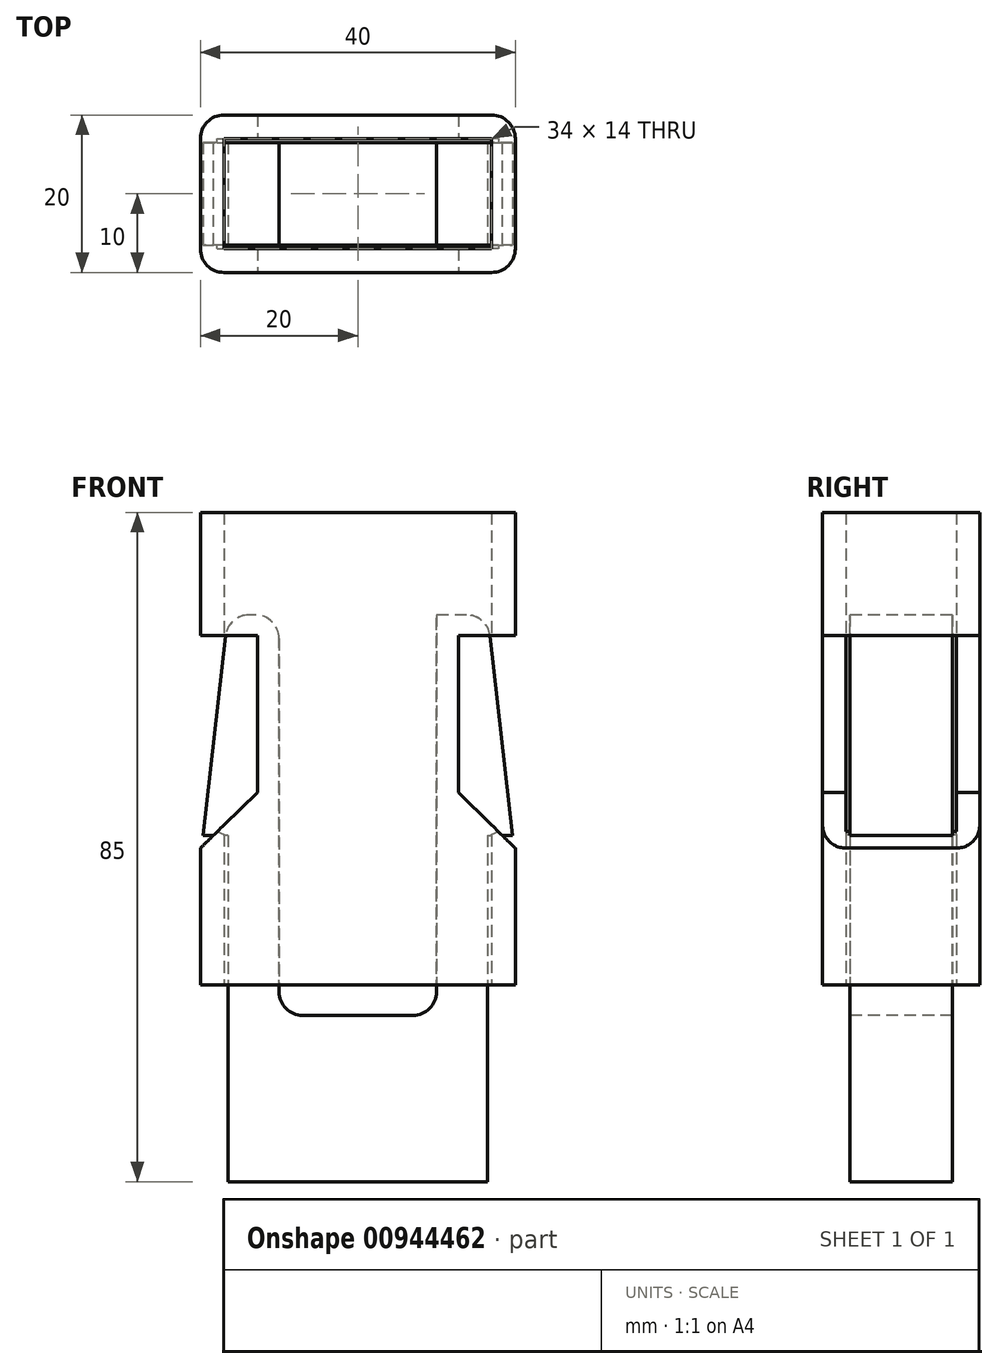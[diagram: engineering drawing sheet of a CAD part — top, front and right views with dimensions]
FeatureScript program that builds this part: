
annotation { "Feature Type Name" : "Feature", "Feature Type Description" : "" }
export const myFeature = defineFeature(function(context is Context, id is Id, definition is map)
    precondition{}
    {
        {
            var Q0;
            Q0=qCreatedBy(makeId("Top.planeOp"),FACE);
            var sketch = newSketch(context, id + "F0", { "sketchPlane" : qUnion([Q0])});
            skLineSegment(sketch, "E0.bottom", {"start": v(17, -10) * mm, "end": v(-17, -10) * mm});
            skLineSegment(sketch, "E0.top", {"start": v(17, 10) * mm, "end": v(-17, 10) * mm});
            skLineSegment(sketch, "E0.left", {"start": v(20, -7) * mm, "end": v(20, 7) * mm});
            skLineSegment(sketch, "E0.right", {"start": v(-20, -7) * mm, "end": v(-20, 7) * mm});
            skPoint(sketch, "E0.middle", {"position": v(0, 0) * mm});
            skPoint(sketch, "E1.visualSharp", {"position": v(-20, 10) * mm});
            skArc(sketch, "E1.filletArc", {"start": v(-17, 10) * mm, "mid": v(-19.12, 9.12) * mm, "end": v(-20, 7) * mm});
            skPoint(sketch, "E2.visualSharp", {"position": v(20, 10) * mm});
            skArc(sketch, "E2.filletArc", {"start": v(20, 7) * mm, "mid": v(19.12, 9.12) * mm, "end": v(17, 10) * mm});
            skPoint(sketch, "E3.visualSharp", {"position": v(20, -10) * mm});
            skArc(sketch, "E3.filletArc", {"start": v(17, -10) * mm, "mid": v(19.12, -9.12) * mm, "end": v(20, -7) * mm});
            skPoint(sketch, "E4.visualSharp", {"position": v(-20, -10) * mm});
            skArc(sketch, "E4.filletArc", {"start": v(-20, -7) * mm, "mid": v(-19.12, -9.12) * mm, "end": v(-17, -10) * mm});
            skLineSegment(sketch, "E5.0", {"start": v(17, 7) * mm, "end": v(-17, 7) * mm});
            skLineSegment(sketch, "E6.0", {"start": v(-17, -7) * mm, "end": v(-17, 7) * mm});
            skLineSegment(sketch, "E7.0", {"start": v(17, -7) * mm, "end": v(-17, -7) * mm});
            skLineSegment(sketch, "E8.0", {"start": v(17, -7) * mm, "end": v(17, 7) * mm});
            skSolve(sketch);
        }
        {
            var Q0;
            Q0=makeQuery(id+"F0.imprint","IMPRINT",FACE,{"disambiguationData":[TD([[makeQuery(id+"F0.imprint","IMPRINT",EDGE,{"derivedFrom":sQuery(id+"F0.wireOp",EDGE,"E0.bottom")}),-1.0]])]});
            extrude(context, id + "F1", {"entities" : qUnion([Q0]), "depth" : 60 * mm, "offsetDistance" : 25 * mm});
        }
        {
            var Q0;
            Q0=qCreatedBy(makeId("Front.planeOp"),FACE);
            var sketch = newSketch(context, id + "F2", { "sketchPlane" : qUnion([Q0])});
            skLineSegment(sketch, "E9", {"start": v(-22.85, 14.58) * mm, "end": v(-12.76, 24.45) * mm});
            skLineSegment(sketch, "E10", {"start": v(-12.76, 24.45) * mm, "end": v(-12.76, 44.4) * mm});
            skLineSegment(sketch, "E11", {"start": v(-12.76, 44.4) * mm, "end": v(-25.04, 44.4) * mm});
            skLineSegment(sketch, "E12", {"start": v(-25.04, 44.4) * mm, "end": v(-22.85, 14.58) * mm});
            skLineSegment(sketch, "E13.MirrorCS", {"start": v(25.04, 44.4) * mm, "end": v(22.85, 14.58) * mm});
            skLineSegment(sketch, "E14.MirrorCS", {"start": v(12.76, 44.4) * mm, "end": v(25.04, 44.4) * mm});
            skLineSegment(sketch, "E15.MirrorCS", {"start": v(12.76, 24.45) * mm, "end": v(12.76, 44.4) * mm});
            skLineSegment(sketch, "E16.MirrorCS", {"start": v(22.85, 14.58) * mm, "end": v(12.76, 24.45) * mm});
            skSolve(sketch);
        }
        {
            var Q0;
            Q0=makeQuery(id+"F2.imprint","IMPRINT",FACE,{"disambiguationData":[TD([[makeQuery(id+"F2.imprint","IMPRINT",EDGE,{"derivedFrom":sQuery(id+"F2.wireOp",EDGE,"E9")}),1.0]])]});
            var Q1;
            Q1=makeQuery(id+"F2.imprint","IMPRINT",FACE,{"disambiguationData":[TD([[makeQuery(id+"F2.imprint","IMPRINT",EDGE,{"derivedFrom":sQuery(id+"F2.wireOp",EDGE,"E13.MirrorCS")}),-1.0]])]});
            extrude(context, id + "F3", {"entities" : qUnion([Q0, Q1]), "operationType" : NewBodyOperationType.REMOVE, "endBound" : BoundingType.SYMMETRIC, "oppositeDirection" : true, "depth" : 25 * mm, "offsetDistance" : 25 * mm});
        }
        {
            var Q0;
            Q0=makeQuery(id+"F1.opExtrude","CAP_FACE",FACE,{"disambiguationData":[OSD([sQuery(id+"F0.wireOp",EDGE,"E0.bottom"),sQuery(id+"F0.wireOp",EDGE,"E0.top"),sQuery(id+"F0.wireOp",EDGE,"E0.left"),sQuery(id+"F0.wireOp",EDGE,"E0.right"),sQuery(id+"F0.wireOp",EDGE,"E1.filletArc"),sQuery(id+"F0.wireOp",EDGE,"E2.filletArc"),sQuery(id+"F0.wireOp",EDGE,"E3.filletArc"),sQuery(id+"F0.wireOp",EDGE,"E4.filletArc"),sQuery(id+"F0.wireOp",EDGE,"E5.0"),sQuery(id+"F0.wireOp",EDGE,"E6.0"),sQuery(id+"F0.wireOp",EDGE,"E7.0"),sQuery(id+"F0.wireOp",EDGE,"E8.0")])],"isStart":true});
            var sketch = newSketch(context, id + "F4", { "sketchPlane" : qUnion([Q0])});
            skLineSegment(sketch, "E17.0", {"start": v(17, 7) * mm, "end": v(-17, 7) * mm, "construction": true});
            skLineSegment(sketch, "E18.0", {"start": v(-17, 7) * mm, "end": v(-17, -7) * mm, "construction": true});
            skLineSegment(sketch, "E19.0", {"start": v(17, -7) * mm, "end": v(-17, -7) * mm, "construction": true});
            skLineSegment(sketch, "E20.0", {"start": v(17, 7) * mm, "end": v(17, -7) * mm, "construction": true});
            skLineSegment(sketch, "E21.0", {"start": v(16.5, 6.5) * mm, "end": v(-16.5, 6.5) * mm});
            skLineSegment(sketch, "E22.0", {"start": v(-16.5, 6.5) * mm, "end": v(-16.5, -6.5) * mm});
            skLineSegment(sketch, "E23.0", {"start": v(16.5, -6.5) * mm, "end": v(-16.5, -6.5) * mm});
            skLineSegment(sketch, "E24.0", {"start": v(16.5, 6.5) * mm, "end": v(16.5, -6.5) * mm});
            skSolve(sketch);
        }
        {
            var Q0;
            Q0=makeQuery(id+"F4.imprint","IMPRINT",FACE,{"disambiguationData":[TD([[makeQuery(id+"F4.imprint","IMPRINT",EDGE,{"derivedFrom":sQuery(id+"F4.wireOp",EDGE,"E21.0")}),1.0]])]});
            extrude(context, id + "F5", {"entities" : qUnion([Q0]), "oppositeDirection" : true, "depth" : 47 * mm, "offsetDistance" : 25 * mm});
        }
        {
            var Q0;
            Q0=makeQuery(id+"F5.opExtrude","CAP_FACE",FACE,{"disambiguationData":[OSD([sQuery(id+"F4.wireOp",EDGE,"E21.0"),sQuery(id+"F4.wireOp",EDGE,"E22.0"),sQuery(id+"F4.wireOp",EDGE,"E23.0"),sQuery(id+"F4.wireOp",EDGE,"E24.0")])],"isStart":true});
            extrude(context, id + "F6", {"entities" : qUnion([Q0]), "operationType" : NewBodyOperationType.ADD, "depth" : 25 * mm, "offsetDistance" : 25 * mm});
        }
        {
            var Q0;
            {var subQ0=sQuery(id+"F4.wireOp",EDGE,"E21.0");Q0=makeQuery(id+"F6.boolean.opBoolean","MERGE",FACE,{"derivedFrom":[makeQuery(id+"F5.opExtrude","SWEPT_FACE",FACE,{"disambiguationData":[OSD([subQ0])]}),makeQuery(id+"F6.opExtrude","SWEPT_FACE",FACE,{"disambiguationData":[OSD([subQ0])]})]});}
            var sketch = newSketch(context, id + "F7", { "sketchPlane" : qUnion([Q0])});
            skLineSegment(sketch, "E25", {"start": v(16.5, 47) * mm, "end": v(19.65, 19) * mm});
            skLineSegment(sketch, "E26", {"start": v(19.65, 19) * mm, "end": v(16.5, 19) * mm});
            skLineSegment(sketch, "E27", {"start": v(16.5, 19) * mm, "end": v(16.5, 47) * mm});
            skLineSegment(sketch, "E28.MirrorCS", {"start": v(-16.5, 47) * mm, "end": v(-19.65, 19) * mm});
            skLineSegment(sketch, "E29.MirrorCS", {"start": v(-16.5, 19) * mm, "end": v(-16.5, 47) * mm});
            skLineSegment(sketch, "E30.MirrorCS", {"start": v(-19.65, 19) * mm, "end": v(-16.5, 19) * mm});
            skSolve(sketch);
        }
        {
            var Q0;
            Q0=makeQuery(id+"F7.imprint","IMPRINT",FACE,{"disambiguationData":[TD([[makeQuery(id+"F7.imprint","IMPRINT",EDGE,{"derivedFrom":sQuery(id+"F7.wireOp",EDGE,"E28.MirrorCS")}),1.0]])]});
            var Q1;
            Q1=makeQuery(id+"F7.imprint","IMPRINT",FACE,{"disambiguationData":[TD([[makeQuery(id+"F7.imprint","IMPRINT",EDGE,{"derivedFrom":sQuery(id+"F7.wireOp",EDGE,"E25")}),-1.0]])]});
            var Q2;
            {var subQ0=sQuery(id+"F4.wireOp",EDGE,"E23.0");Q2=makeQuery(id+"F6.boolean.opBoolean","MERGE",FACE,{"derivedFrom":[makeQuery(id+"F5.opExtrude","SWEPT_FACE",FACE,{"disambiguationData":[OSD([subQ0])]}),makeQuery(id+"F6.opExtrude","SWEPT_FACE",FACE,{"disambiguationData":[OSD([subQ0])]})]});}
            extrude(context, id + "F8", {"entities" : qUnion([Q0, Q1]), "operationType" : NewBodyOperationType.ADD, "endBound" : BoundingType.UP_TO_SURFACE, "oppositeDirection" : true, "depth" : 25 * mm, "endBoundEntityFace" : qUnion([Q2]), "offsetDistance" : 25 * mm});
        }
        {
            var Q0;
            {var subQ0=sQuery(id+"F4.wireOp",EDGE,"E21.0");Q0=makeQuery(id+"F8.boolean.opBoolean","MERGE",FACE,{"derivedFrom":[makeQuery(id+"F6.boolean.opBoolean","MERGE",FACE,{"derivedFrom":[makeQuery(id+"F5.opExtrude","SWEPT_FACE",FACE,{"disambiguationData":[OSD([subQ0])]}),makeQuery(id+"F6.opExtrude","SWEPT_FACE",FACE,{"disambiguationData":[OSD([subQ0])]})]}),makeQuery(id+"F8.opExtrude","CAP_FACE",FACE,{"disambiguationData":[OSD([sQuery(id+"F7.wireOp",EDGE,"E25"),sQuery(id+"F7.wireOp",EDGE,"E26"),sQuery(id+"F7.wireOp",EDGE,"E27")])],"isStart":true}),makeQuery(id+"F8.opExtrude","CAP_FACE",FACE,{"disambiguationData":[OSD([sQuery(id+"F7.wireOp",EDGE,"E28.MirrorCS"),sQuery(id+"F7.wireOp",EDGE,"E29.MirrorCS"),sQuery(id+"F7.wireOp",EDGE,"E30.MirrorCS")])],"isStart":true})]});}
            var sketch = newSketch(context, id + "F9", { "sketchPlane" : qUnion([Q0])});
            skLineSegment(sketch, "E31", {"start": v(-10, 19) * mm, "end": v(-10, -3.9) * mm});
            skLineSegment(sketch, "E32", {"start": v(-10, -3.9) * mm, "end": v(0, -3.9) * mm});
            skLineSegment(sketch, "E33", {"start": v(0, -3.9) * mm, "end": v(0, 54.54) * mm});
            skPoint(sketch, "E33.endSnap0", {"position": v(0, 47) * mm});
            skLineSegment(sketch, "E34", {"start": v(0, 54.54) * mm, "end": v(-10, 54.54) * mm});
            skLineSegment(sketch, "E35", {"start": v(-10, 54.54) * mm, "end": v(-10, 19) * mm});
            skLineSegment(sketch, "E36.MirrorCS", {"start": v(0, 54.54) * mm, "end": v(10, 54.54) * mm});
            skLineSegment(sketch, "E37.MirrorCS", {"start": v(10, 54.54) * mm, "end": v(10, 19) * mm});
            skLineSegment(sketch, "E38.MirrorCS", {"start": v(10, 19) * mm, "end": v(10, -3.9) * mm});
            skLineSegment(sketch, "E39.MirrorCS", {"start": v(10, -3.9) * mm, "end": v(0, -3.9) * mm});
            skSolve(sketch);
        }
        {
            var Q0;
            {var subQ5=sQuery(id+"F9.wireOp",EDGE,"E31");Q0=makeQuery(id+"F9.imprint","IMPRINT",FACE,{"disambiguationData":[TD([[makeQuery(id+"F9.imprint","IMPRINT",EDGE,{"derivedFrom":subQ5}),1.0]])]});}
            var Q1;
            {var subQ0=sQuery(id+"F9.wireOp",EDGE,"E34");Q1=makeQuery(id+"F9.imprint","IMPRINT",FACE,{"disambiguationData":[TD([[makeQuery(id+"F9.imprint","IMPRINT",EDGE,{"derivedFrom":subQ0}),1.0]])]});}
            var Q2;
            {var subQ0=sQuery(id+"F9.wireOp",EDGE,"E36.MirrorCS");Q2=makeQuery(id+"F9.imprint","IMPRINT",FACE,{"disambiguationData":[TD([[makeQuery(id+"F9.imprint","IMPRINT",EDGE,{"derivedFrom":subQ0}),-1.0]])]});}
            var Q3;
            {var subQ6=sQuery(id+"F9.wireOp",EDGE,"E38.MirrorCS");Q3=makeQuery(id+"F9.imprint","IMPRINT",FACE,{"disambiguationData":[TD([[makeQuery(id+"F9.imprint","IMPRINT",EDGE,{"derivedFrom":subQ6}),-1.0]])]});}
            extrude(context, id + "F10", {"entities" : qUnion([Q0, Q1, Q2, Q3]), "operationType" : NewBodyOperationType.REMOVE, "endBound" : BoundingType.UP_TO_NEXT, "oppositeDirection" : true, "depth" : 25 * mm, "offsetDistance" : 25 * mm});
        }
        {
            var Q0;
            Q0=makeQuery(id+"F8.boolean.opBoolean","MERGE",EDGE,{"derivedFrom":[makeQuery(id+"F5.opExtrude","CAP_EDGE",EDGE,{"disambiguationData":[OSD([sQuery(id+"F4.wireOp",EDGE,"E24.0")])],"isStart":false}),makeQuery(id+"F8.opExtrude","SWEPT_EDGE",EDGE,{"disambiguationData":[OSD([sQuery(id+"F4.wireOp",EDGE,"E21.0"),sQuery(id+"F7.wireOp",EDGE,"E25"),sQuery(id+"F7.wireOp",EDGE,"E27")])]})]});
            var Q1;
            Q1=makeQuery(id+"F10.boolean.opBoolean","COPY",EDGE,{"derivedFrom":makeQuery(id+"F10.opExtrude","CAP_EDGE",EDGE,{"disambiguationData":[OSD([sQuery(id+"F9.wireOp",EDGE,"E37.MirrorCS"),sQuery(id+"F9.wireOp",EDGE,"E38.MirrorCS")]),topologyDisambiguationEdgeConnected([makeQuery(id+"F5.opExtrude","CAP_FACE",FACE,{"disambiguationData":[OSD([sQuery(id+"F4.wireOp",EDGE,"E21.0"),sQuery(id+"F4.wireOp",EDGE,"E22.0"),sQuery(id+"F4.wireOp",EDGE,"E23.0"),sQuery(id+"F4.wireOp",EDGE,"E24.0")])],"isStart":false})])],"isStart":false})});
            var Q2;
            Q2=makeQuery(id+"F8.boolean.opBoolean","MERGE",EDGE,{"derivedFrom":[makeQuery(id+"F5.opExtrude","CAP_EDGE",EDGE,{"disambiguationData":[OSD([sQuery(id+"F4.wireOp",EDGE,"E22.0")])],"isStart":false}),makeQuery(id+"F8.opExtrude","SWEPT_EDGE",EDGE,{"disambiguationData":[OSD([sQuery(id+"F4.wireOp",EDGE,"E21.0"),sQuery(id+"F7.wireOp",EDGE,"E28.MirrorCS"),sQuery(id+"F7.wireOp",EDGE,"E29.MirrorCS")])]})]});
            var Q3;
            Q3=makeQuery(id+"F10.boolean.opBoolean","COPY",EDGE,{"derivedFrom":makeQuery(id+"F10.opExtrude","CAP_EDGE",EDGE,{"disambiguationData":[OSD([sQuery(id+"F9.wireOp",EDGE,"E31"),sQuery(id+"F9.wireOp",EDGE,"E35")]),topologyDisambiguationEdgeConnected([makeQuery(id+"F5.opExtrude","CAP_FACE",FACE,{"disambiguationData":[OSD([sQuery(id+"F4.wireOp",EDGE,"E21.0"),sQuery(id+"F4.wireOp",EDGE,"E22.0"),sQuery(id+"F4.wireOp",EDGE,"E23.0"),sQuery(id+"F4.wireOp",EDGE,"E24.0")])],"isStart":false})])],"isStart":false})});
            var Q4;
            Q4=makeQuery(id+"F10.boolean.opBoolean","COPY",EDGE,{"derivedFrom":makeQuery(id+"F10.opExtrude","SWEPT_EDGE",EDGE,{"disambiguationData":[OSD([sQuery(id+"F9.wireOp",EDGE,"E31"),sQuery(id+"F9.wireOp",EDGE,"E32")])]})});
            var Q5;
            Q5=makeQuery(id+"F10.boolean.opBoolean","COPY",EDGE,{"derivedFrom":makeQuery(id+"F10.opExtrude","SWEPT_EDGE",EDGE,{"disambiguationData":[OSD([sQuery(id+"F9.wireOp",EDGE,"E38.MirrorCS"),sQuery(id+"F9.wireOp",EDGE,"E39.MirrorCS")])]})});
            fillet(context, id + "F11", {"entities" : qUnion([Q0, Q1, Q2, Q3, Q4, Q5]), "radius" : 3 * mm, "tangentPropagation" : true, "allowEdgeOverflow" : false});
        }
        {
            var Q0;
            Q0=makeQuery(id+"F3.boolean.opBoolean","INTERSECT",EDGE,{"derivedFrom":[makeQuery(id+"F1.opExtrude","SWEPT_FACE",FACE,{"disambiguationData":[OSD([sQuery(id+"F0.wireOp",EDGE,"E8.0")])]}),makeQuery(id+"F3.opExtrude","SWEPT_FACE",FACE,{"disambiguationData":[OSD([sQuery(id+"F2.wireOp",EDGE,"E16.MirrorCS")])]})]});
            var Q1;
            Q1=makeQuery(id+"F3.boolean.opBoolean","INTERSECT",EDGE,{"derivedFrom":[makeQuery(id+"F1.opExtrude","SWEPT_FACE",FACE,{"disambiguationData":[OSD([sQuery(id+"F0.wireOp",EDGE,"E6.0")])]}),makeQuery(id+"F3.opExtrude","SWEPT_FACE",FACE,{"disambiguationData":[OSD([sQuery(id+"F2.wireOp",EDGE,"E9")])]})]});
            chamfer(context, id + "F12", {"entities" : qUnion([Q0, Q1]), "width" : 0.5 * mm, "tangentPropagation" : true});
        }
    });
